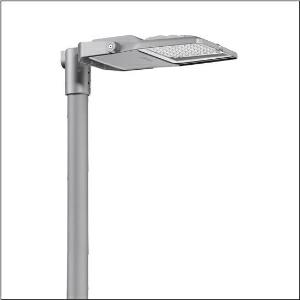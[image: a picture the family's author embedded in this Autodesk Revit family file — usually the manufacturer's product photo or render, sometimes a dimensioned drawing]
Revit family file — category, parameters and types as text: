
# Revit family: floodlight_fl_21_mini___pl43_5xa7776d2a3a_6ee6
name_source: partatom
category: Lighting Fixtures
units: mm (PartAtom-declared; Revit-internal decimal feet)

## family parameters
Cut with Voids When Loaded = No
Host = Face
Light Source = No
Part Type = Normal
Room Calculation Point = No
Round Connector Dimension = Use Diameter
Shared = No

## types (1)
- --- (1 x LED, 18300 lm, 142.9 W, 3000K)
    Apparent Load = 143 VA
    CIE Flux Codes = 27 78 99 100 100
    Color Rendering = 70
    Color Temperature = 3000K
    Default Elevation = 1800 mm
    Description = Floodlight FL 21 mini, floodlight, primary light control with lens, of PMMA, primary optical cover: protective disc, of toughened safety glass, transparent, light distribution: PL43, light emission: direct distribution, installation type: surface-mounted, LED, High Power LED, rated luminous flux: 18.300lm, luminous efficacy: 128lm/W, light colour: 730, colour temperature: 3000K, control: flexible luminous flux parameterisation, time-dependent luminous flux control, constant luminous flux control, overheat protection, presetting dimming logarithmic, with terminal, 6-pole, mains connection: 220..240V, AC, 50/60Hz, start of lifetime: 143W, end of service life: 151W, reduction: 63W, luminaire housing, of diecast aluminium, powder-coated, Siteco® metallic grey (DB 702S), corrosivity category C5 mid according to DIN EN ISO 12944, sealing non-destructively replaceable, please order mast flange separately, mast bracket, of steel, galvanised, powder-coated, Siteco® metallic grey (DB 702S), Smart Interface below and above, protection rating (complete): IP66, insulation class (complete): insulation class II (safety insulation), certification: CE, ENEC, VDE, protection symbol: D, impact resistance: IK08, permissible operating ambient temperature: -40..+40°C, permissible operating ambient temperature for outdoor applications: -40..+50°C, standard: DIN EN 12944, LABS conformity tested according to VDMA 24364:2018-05, packaging unit: 1 piece

Light Distribution: PL43
    Height = 70 mm
    Lamp = 1 x LED
    Lamp Light Flux = 18300 lm
    Lamp Power = 142.9 W
    Lamp count = 1
    Length = 485 mm
    Luminous efficacy = 128 lm/W
    Manufacturer = Siteco
    ModVariant = No
    Model = 5XA7776D2A3A
    Number of Poles = 1
    OnlyDefault = Yes
    Power Factor = 1
    Product Name = Floodlight FL 21 mini | PL43
    Product group = floodlight | pylon annexe
    ProductGroupID = 6200
    Protection Class = Protection class II
    Protection Degree = IP 66
    RLX_Detail_Level = 1
    RLX_Emergency_Light_Flux = 0 lm
    RLX_Emergency_Type = 0
    RLX_Emergency_Type_DB = No
    RlxData = <blob elided: 101201 chars, md5=a01576ef>
    Socket = socket
    Standby Power = 0 W
    System Light Flux = 18300 lm
    System Power = 143 W
    Type Comments = factory setting: luminous flux: 100 % | dim-lin: 254 | 730 mA
    Type Image = l_1007125.jpg
    URL = http://relux.com
    VarID = @adj_093251
    Voltage = 0 V
    Weight = 0.00 kg
    Width = 337 mm

## geometry (parser evidence)
native form markers: Blend x4, Sweep x11
no freeform markers — native parametric forms only
